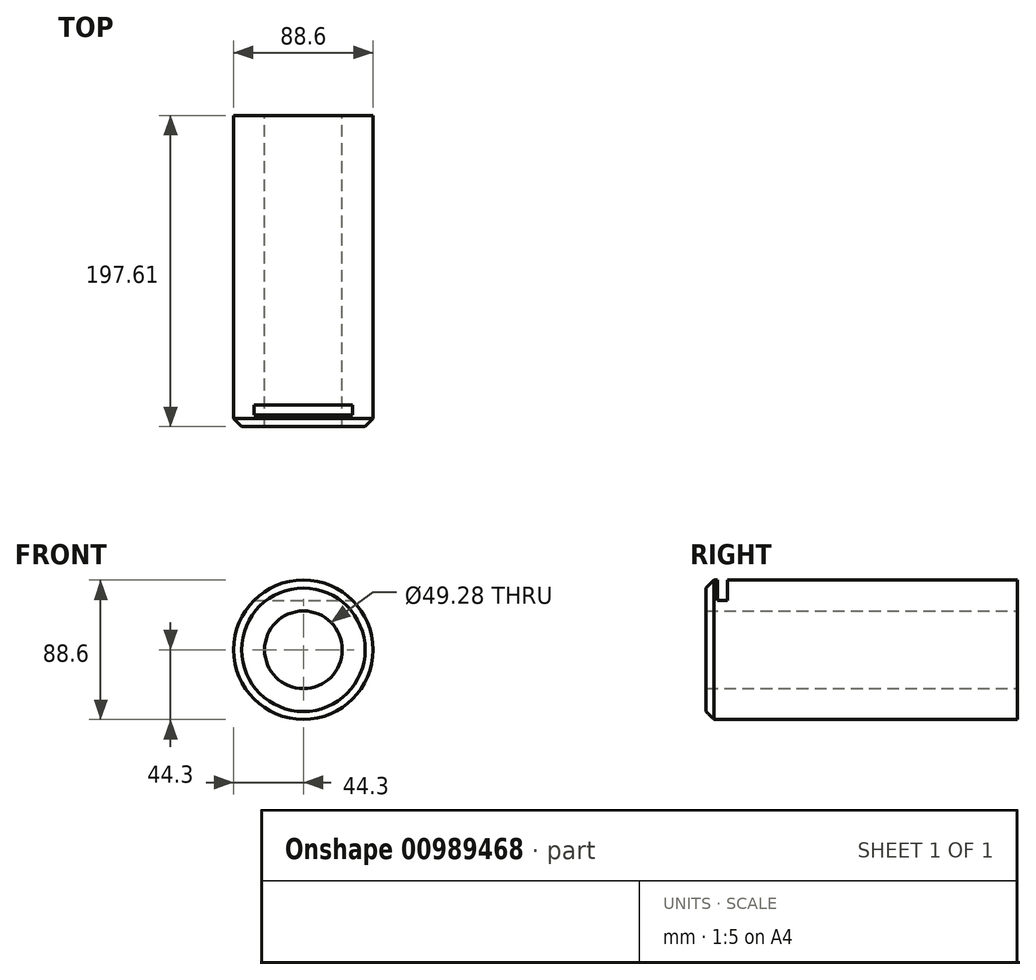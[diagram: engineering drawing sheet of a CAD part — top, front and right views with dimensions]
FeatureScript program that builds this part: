
annotation { "Feature Type Name" : "Feature", "Feature Type Description" : "" }
export const myFeature = defineFeature(function(context is Context, id is Id, definition is map)
    precondition{}
    {
        {
            var Q0;
            Q0=qCreatedBy(makeId("Front.planeOp"),FACE);
            var sketch = newSketch(context, id + "F0", { "sketchPlane" : qUnion([Q0])});
            skCircle(sketch, "E0", {"center": v(0, 0) * mm, "radius": 44.3 * mm});
            skCircle(sketch, "E1", {"center": v(0, 0) * mm, "radius": 24.64 * mm});
            skSolve(sketch);
        }
        {
            var Q0;
            Q0=makeQuery(id+"F0.imprint","IMPRINT",FACE,{"disambiguationData":[TD([[makeQuery(id+"F0.imprint","IMPRINT",EDGE,{"derivedFrom":sQuery(id+"F0.wireOp",EDGE,"E0")}),1.0]])]});
            extrude(context, id + "F1", {"entities" : qUnion([Q0]), "depth" : 197.61 * mm, "offsetDistance" : 25.4 * mm});
        }
        {
            var Q0;
            Q0=qCreatedBy(makeId("Top.planeOp"),FACE);
            cPlane(context, id + "F2", {"entities" : qUnion([Q0]), "cplaneType" : CPlaneType.OFFSET, "offset" : 44.3 * mm, "width" : 152.4 * mm, "height" : 152.4 * mm});
        }
        {
            var Q0;
            Q0=qCreatedBy(id+"F2.planeOp",FACE);
            var sketch = newSketch(context, id + "F3", { "sketchPlane" : qUnion([Q0])});
            skLineSegment(sketch, "E2.bottom", {"start": v(-44.45, -183.9) * mm, "end": v(44.45, -183.9) * mm});
            skLineSegment(sketch, "E2.top", {"start": v(-44.45, -190.37) * mm, "end": v(44.45, -190.37) * mm});
            skLineSegment(sketch, "E2.left", {"start": v(-44.45, -183.9) * mm, "end": v(-44.45, -190.37) * mm});
            skLineSegment(sketch, "E2.right", {"start": v(44.45, -183.9) * mm, "end": v(44.45, -190.37) * mm});
            skSolve(sketch);
        }
        {
            var Q0;
            Q0 = qSketchRegion(id + "F3", true);
            extrude(context, id + "F4", {"entities" : qUnion([Q0]), "operationType" : NewBodyOperationType.REMOVE, "oppositeDirection" : true, "depth" : 12.83 * mm, "offsetDistance" : 25.4 * mm});
        }
        {
            var Q0;
            Q0=makeQuery(id+"F1.opExtrude","CAP_EDGE",EDGE,{"disambiguationData":[OSD([sQuery(id+"F0.wireOp",EDGE,"E0")])],"isStart":false});
            chamfer(context, id + "F5", {"entities" : qUnion([Q0]), "width" : 5.08 * mm});
        }
    });
